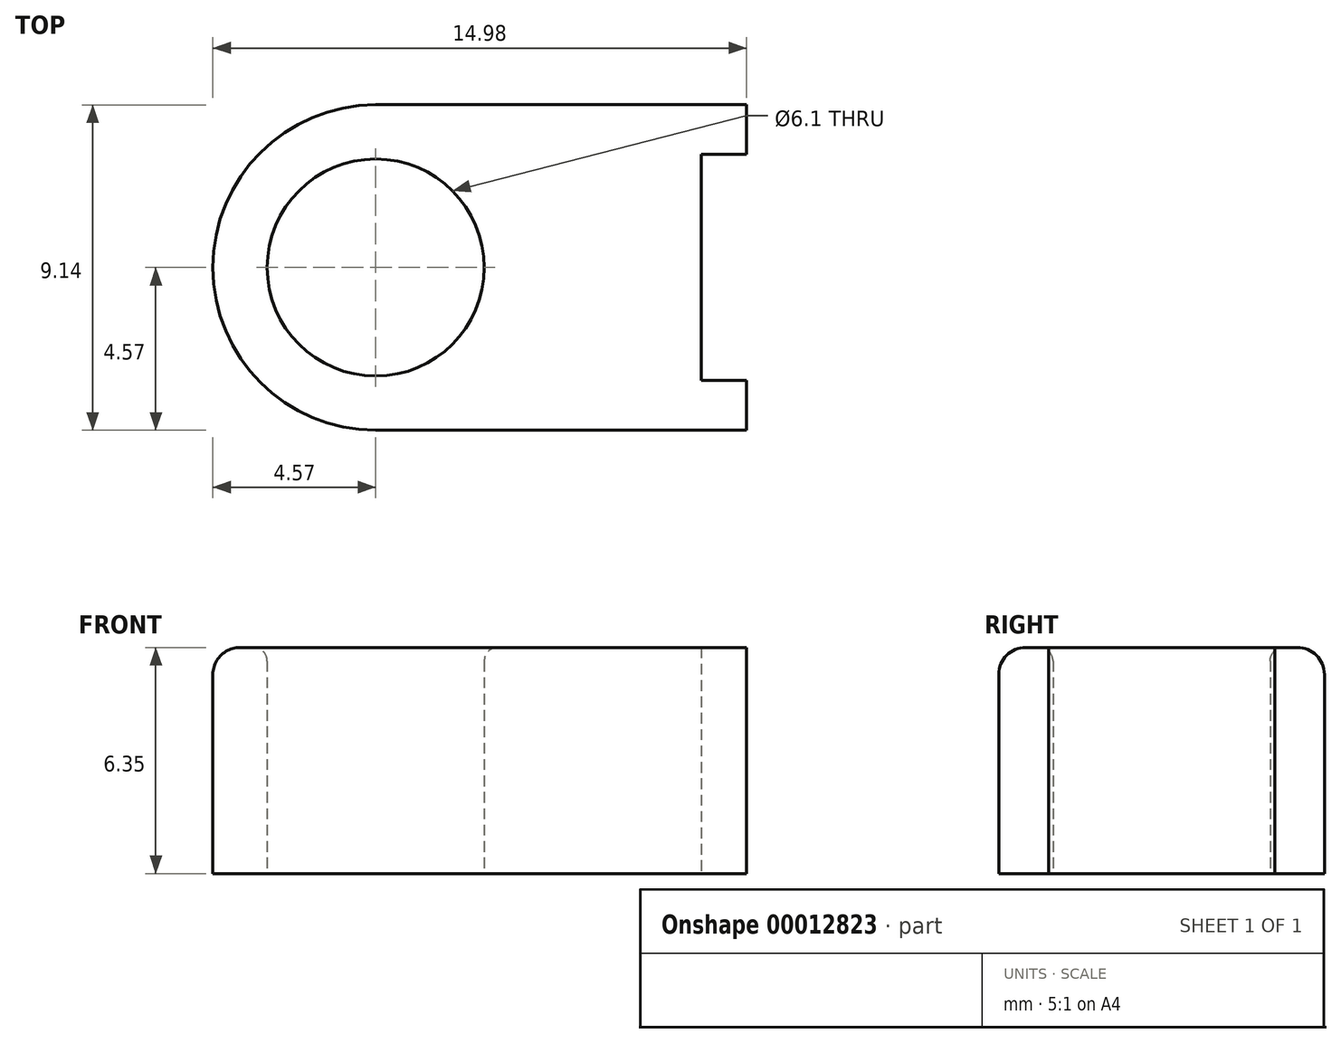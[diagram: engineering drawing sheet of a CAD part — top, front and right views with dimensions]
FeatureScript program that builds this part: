
annotation { "Feature Type Name" : "Feature", "Feature Type Description" : "" }
export const myFeature = defineFeature(function(context is Context, id is Id, definition is map)
    precondition{}
    {
        {
            var Q0;
            Q0=qCreatedBy(makeId("Top.planeOp"),FACE);
            var sketch = newSketch(context, id + "F0", { "sketchPlane" : qUnion([Q0])});
            skCircle(sketch, "E0", {"center": v(0, 0) * mm, "radius": 3.05 * mm});
            skCircle(sketch, "E1", {"center": v(0, 0) * mm, "radius": 4.57 * mm});
            skLineSegment(sketch, "E2", {"start": v(0, -4.57) * mm, "end": v(10.41, -4.57) * mm});
            skLineSegment(sketch, "E3", {"start": v(10.41, -4.57) * mm, "end": v(10.41, -3.18) * mm});
            skLineSegment(sketch, "E4", {"start": v(10.41, -3.18) * mm, "end": v(9.14, -3.18) * mm});
            skLineSegment(sketch, "E5", {"start": v(9.14, -3.18) * mm, "end": v(9.14, 0) * mm});
            skLineSegment(sketch, "E6", {"start": v(0, 0) * mm, "end": v(9.14, 0) * mm, "construction": true});
            skLineSegment(sketch, "E7.MirrorCS", {"start": v(0, 4.57) * mm, "end": v(10.41, 4.57) * mm});
            skLineSegment(sketch, "E8.MirrorCS", {"start": v(10.41, 3.18) * mm, "end": v(9.14, 3.18) * mm});
            skLineSegment(sketch, "E9.MirrorCS", {"start": v(9.14, 3.18) * mm, "end": v(9.14, 0) * mm});
            skLineSegment(sketch, "E10.MirrorCS", {"start": v(10.41, 4.57) * mm, "end": v(10.41, 3.18) * mm});
            skSolve(sketch);
        }
        {
            var Q0;
            {var subQ0=sQuery(id+"F0.wireOp",EDGE,"E2");Q0=makeQuery(id+"F0.imprint","IMPRINT",FACE,{"disambiguationData":[TD([[makeQuery(id+"F0.imprint","IMPRINT",EDGE,{"derivedFrom":subQ0}),1.0]])]});}
            var Q1;
            Q1=makeQuery(id+"F0.imprint","IMPRINT",FACE,{"disambiguationData":[TD([[makeQuery(id+"F0.imprint","IMPRINT",EDGE,{"derivedFrom":sQuery(id+"F0.wireOp",EDGE,"E0")}),-1.0]])]});
            extrude(context, id + "F1", {"entities" : qUnion([Q0, Q1]), "depth" : 6.35 * mm, "offsetDistance" : 25.4 * mm});
        }
        {
            var Q0;
            Q0=makeQuery(id+"F1.opExtrude","CAP_EDGE",EDGE,{"disambiguationData":[OSD([sQuery(id+"F0.wireOp",EDGE,"E7.MirrorCS")])],"isStart":false});
            fillet(context, id + "F2", {"entities" : qUnion([Q0]), "radius" : 0.76 * mm, "tangentPropagation" : true, "allowEdgeOverflow" : false});
        }
        {
            var Q0;
            Q0=makeQuery(id+"F1.opExtrude","CAP_EDGE",EDGE,{"disambiguationData":[OSD([sQuery(id+"F0.wireOp",EDGE,"E0")])],"isStart":false});
            fillet(context, id + "F3", {"entities" : qUnion([Q0]), "radius" : 0.38 * mm, "tangentPropagation" : true, "allowEdgeOverflow" : false});
        }
    });
